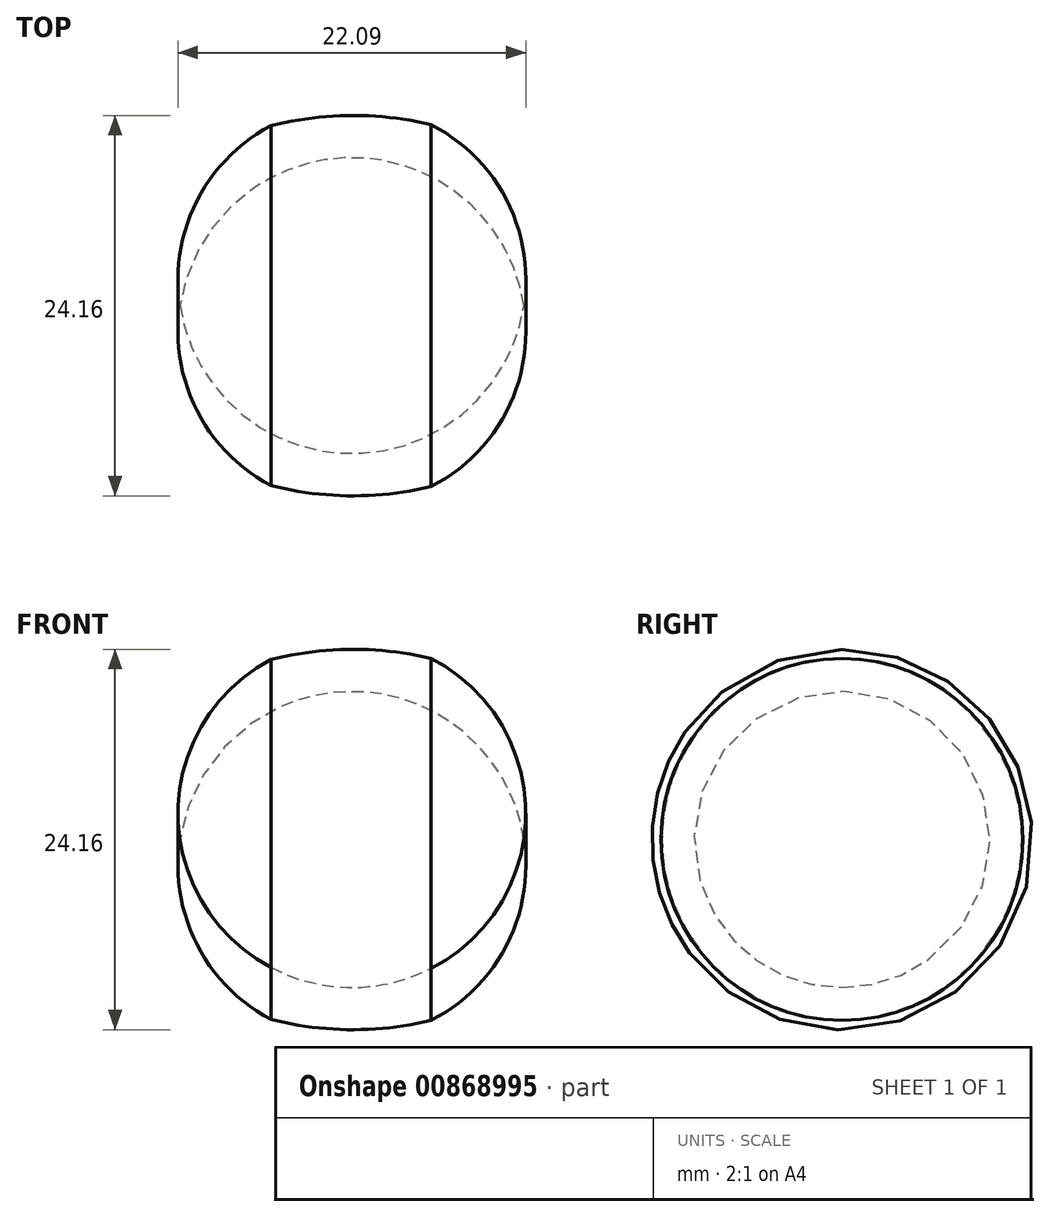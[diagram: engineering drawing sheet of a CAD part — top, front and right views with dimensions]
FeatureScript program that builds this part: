
annotation { "Feature Type Name" : "Feature", "Feature Type Description" : "" }
export const myFeature = defineFeature(function(context is Context, id is Id, definition is map)
    precondition{}
    {
        {
            var Q0;
            Q0=qCreatedBy(makeId("Front.planeOp"),FACE);
            var sketch = newSketch(context, id + "F0", { "sketchPlane" : qUnion([Q0])});
            skArc(sketch, "E0", {"start": v(4.99, 11.5) * mm, "mid": v(-0.1, 12.7) * mm, "end": v(-5.17, 11.43) * mm});
            skArc(sketch, "E1", {"start": v(4.99, 11.5) * mm, "mid": v(-0.1, 12.08) * mm, "end": v(-5.17, 11.43) * mm});
            skLineSegment(sketch, "E2", {"start": v(-1.71, 0) * mm, "end": v(2.14, 0) * mm});
            skSolve(sketch);
        }
        {
            var Q0;
            Q0 = qSketchRegion(id + "F0", true);
            var Q1;
            Q1=sQuery(id+"F0.wireOp",EDGE,"E2");
            revolve(context, id + "F1", {"surfaceOperationType" : NewSurfaceOperationType.NEW, "entities" : qUnion([Q0]), "axis" : qUnion([Q1]), "revolveType" : RevolveType.FULL});
        }
    });
